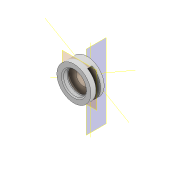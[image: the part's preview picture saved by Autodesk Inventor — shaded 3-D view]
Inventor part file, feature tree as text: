
AUTODESK INVENTOR PART (.ipt)
format: ipt  version: 2022 (Build 260153000, 153)  size: 202,240 bytes
history: native  units: mm
features: other x6, sketch x4, extrude x3, reference x3, plane x2, chamfer x2, revolve x1, pattern_circular x1, projected_geometry x1
ambient origin geometry x8: Origin, YZ Plane, XZ Plane, XY Plane, X Axis, Y Axis, Z Axis, Center Point
bodies: Volumenkörper1 (feature_tree)
feature tree (23):
  plane  "Arbeitsebene1"
  revolve  "Umdrehung1"
  extrude  "Extrusion1"  Depth=1.0mm
  pattern_circular  "Runde Anordnung1"  Count=3 Angle=360.0deg
  chamfer  "Fase1"  Distance=0.5mm
  other  "Arbeitsachse1"
  other  "Arbeitsachse2"
  other  "Arbeitsachse3"
  extrude  "Extrusion4"  Depth=15.0mm
  chamfer  "Fase3"  Distance=1.0mm Angle=45.0deg
  plane  "Arbeitsebene3"
  extrude  "Extrusion5"  Depth=26.0mm
  sketch  "Skizze1"  dims[d1=12.0mm d3=1.0mm]
  reference  "Referenz4"
  sketch  "Skizze2"  dims[d4=360.0deg]
  reference  "Referenz5"
  reference  "Referenz6"
  sketch  "Skizze6"  dims[d5=2.8mm]
  projected_geometry  "Projizierte Kontur1"
  sketch  "Skizze7"  dims[d6=10.0mm d7=0.0mm d8=30.0mm d9=360.0deg d11=0.5mm d13=15.0mm d16=1.0mm d17=2.0mm d18=45.0deg d31=20.1mm d32=5.0mm d33=0.0mm d34=1.0mm d35=2.0mm d36=45.0deg d37=0.3mm d38=6.396926mm d39=-5.0mm d40=26.0mm d41=0.5mm d42=0.0mm d43=3.5mm d44=0.0mm]
  other  "Assembly_Cube_Z-Stage_NEMA11_universal.iam"
  other  "30_Linear_Stage_NEMA11_arm_bayonetmount_v0:1"
  other  "Baugruppe2"
